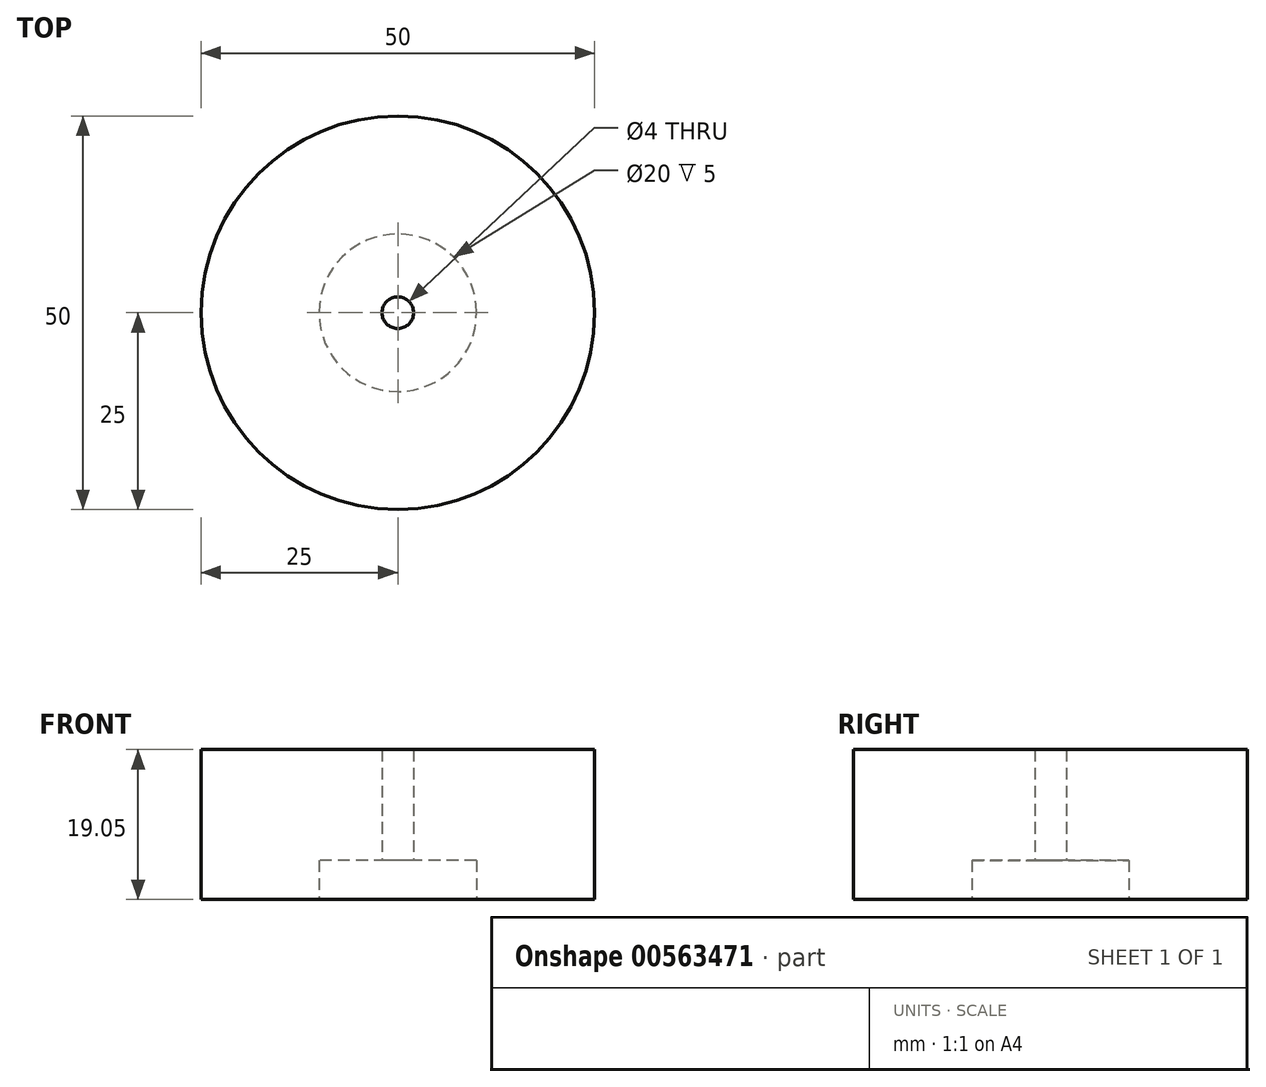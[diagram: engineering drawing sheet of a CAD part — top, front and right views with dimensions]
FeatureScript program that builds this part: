
annotation { "Feature Type Name" : "Feature", "Feature Type Description" : "" }
export const myFeature = defineFeature(function(context is Context, id is Id, definition is map)
    precondition{}
    {
        {
            var Q0;
            Q0=qCreatedBy(makeId("Top.planeOp"),FACE);
            var sketch = newSketch(context, id + "F0", { "sketchPlane" : qUnion([Q0])});
            skCircle(sketch, "E0", {"center": v(0, 0) * mm, "radius": 25 * mm});
            skCircle(sketch, "E1", {"center": v(0, 0) * mm, "radius": 2 * mm});
            skCircle(sketch, "E2", {"center": v(0, 0) * mm, "radius": 10 * mm});
            skSolve(sketch);
        }
        {
            var Q0;
            Q0=makeQuery(id+"F0.imprint","IMPRINT",FACE,{"disambiguationData":[TD([[makeQuery(id+"F0.imprint","IMPRINT",EDGE,{"derivedFrom":sQuery(id+"F0.wireOp",EDGE,"E0")}),1.0]])]});
            var Q1;
            Q1=makeQuery(id+"F0.imprint","IMPRINT",FACE,{"disambiguationData":[TD([[makeQuery(id+"F0.imprint","IMPRINT",EDGE,{"derivedFrom":sQuery(id+"F0.wireOp",EDGE,"E1")}),-1.0]])]});
            extrude(context, id + "F1", {"entities" : qUnion([Q0, Q1]), "depth" : 19.05 * mm, "offsetDistance" : 25 * mm});
        }
        {
            var Q0;
            Q0=makeQuery(id+"F0.imprint","IMPRINT",FACE,{"disambiguationData":[TD([[makeQuery(id+"F0.imprint","IMPRINT",EDGE,{"derivedFrom":sQuery(id+"F0.wireOp",EDGE,"E1")}),-1.0]])]});
            extrude(context, id + "F2", {"entities" : qUnion([Q0]), "operationType" : NewBodyOperationType.REMOVE, "depth" : 5 * mm, "offsetDistance" : 25 * mm});
        }
    });
